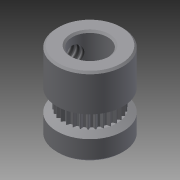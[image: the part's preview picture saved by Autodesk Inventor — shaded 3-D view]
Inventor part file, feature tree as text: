
AUTODESK INVENTOR PART (.ipt)
format: ipt  version: 2014 (Build 180170000, 170)  size: 381,952 bytes
history: native  units: mm
features: sketch x7, extrude x4, plane x3, revolve x1, hole x1, chamfer x1, other x1, fillet x1, pattern_circular x1
ambient origin geometry x8: Origin, YZ Plane, XZ Plane, XY Plane, X Axis, Y Axis, Z Axis, Center Point
bodies: Solid1 (feature_tree)
feature tree (20):
  extrude  "Extrusion1"  Depth=11.0mm
  extrude  "Extrusion2"  Depth=5.0mm
  plane  "Work Plane1"
  revolve  "Revolution1"  [1 undecoded]
  hole  "Hole1"  [1 undecoded]
  chamfer  "Chamfer1"  Distance=1.0mm
  other  "Work Axis1"
  extrude  "Extrusion5"  TaperAngle=30.0deg  [1 undecoded]
  fillet  "Fillet1"  Radius=2.0mm
  pattern_circular  "Circular Pattern1"  [2 undecoded]
  plane  "Work Plane2"
  sketch  "Sketch5"  dims[d6=-4.3mm]
  extrude  "Extrusion4"  TaperAngle=90.0deg  [1 undecoded]
  sketch  "Sketch1"  dims[d0=9.4mm d1=11.0mm]
  sketch  "Sketch2"  dims[d2=0.0mm d3=5.0mm]
  sketch  "Sketch4"  dims[d4=11.0mm d5=0.0mm]
  sketch  "Sketch6"  dims[d11=2.642mm d12=6.0mm d13=3.023mm d14=2.0mm d15=14.3117mm d16=8.0mm d17=20.594885mm d18=1.0mm]
  sketch  "Sketch7"  dims[d19=9.4mm d20=1.0mm d21=0.0mm]
  sketch  "Sketch8"  dims[d22=30.0deg d23=30.0deg d24=2.0mm d25=3.789877mm d26=90.0deg d27=0.25mm d28=2.0mm d29=45.0deg d30=120.0deg d31=120.0deg d32=0.714375mm d33=0.4mm d34=2.0mm d35=0.0mm d36=0.05mm d37=300.0mm d38=360.0deg]
  plane  "Work Plane3"
note: 6 required parameter values undecoded (feature->parameter linkage not recoverable at this tier; creation-order binding heuristic only, values carry confidence <= 0.55)